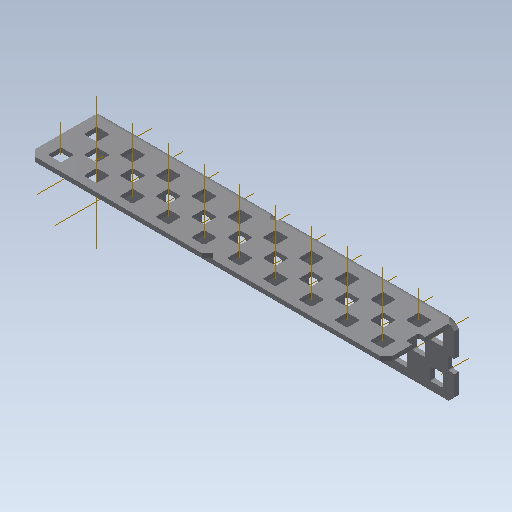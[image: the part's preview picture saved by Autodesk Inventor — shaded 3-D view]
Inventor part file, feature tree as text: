
AUTODESK INVENTOR PART (.ipt)
format: ipt  version: 2020 (Build 240168000, 168)  size: 1,934,336 bytes
history: native  units: in
note: dims shown in document units (in); Inventor stores cm internally (conversion verified against a paired STEP export)
features: other x65, pattern_linear x4, sheet_metal_op x1, extrude x1, imported_body x1, sketch x1
ambient origin geometry x8: Origin, YZ Plane, XZ Plane, XY Plane, X Axis, Y Axis, Z Axis, Center Point
bodies: Body1 (feature_tree)
feature tree (73):
  sheet_metal_op  "Fold1"
  other  "L-Channel"
  extrude  "length cut"  Depth=0.5in
  other  "top out axis"
  other  "top inner axis"
  other  "back out axis"
  other  "back inner axis"
  pattern_linear  "top outer axes"  Count1=2 Spacing1=0.5in
  pattern_linear  "top inner axes"  Spacing1=0.5in  [1 undecoded]
  pattern_linear  "back outer axes"  Count1=2 Spacing1=0.5in
  pattern_linear  "back inner axes"  Spacing1=0.5in  [1 undecoded]
  other  "right plane"
  imported_body  "Base1"
  sketch  "Sketch1"  dims[d1=0.0in d4=0.5in d5=0.7874in d7=0.5in d10=0.5in d13=0.5in d14=0.7874in d16=0.5in d19=0.5in d20=-5.0in d21=0.0in d22=0.0in d23=0.0in d24=0.0in d25=0.0in d26=0.0in]
  other  "Work Point1"
  other  "Work Point2"
  other  "Work Point3"
  other  "Work Point4"
  other  "Work Axis5"
  other  "Work Axis6"
  other  "Work Axis7"
  other  "Work Axis8"
  other  "Work Axis11"
  other  "Work Axis12"
  other  "Work Axis13"
  other  "Work Axis14"
  other  "Work Axis15"
  other  "Work Axis18"
  other  "Work Axis19"
  other  "Work Axis20"
  other  "Work Axis23"
  other  "Work Axis24"
  other  "Work Axis25"
  other  "Work Axis26"
  other  "Work Axis29"
  other  "Work Axis30"
  other  "Work Axis31"
  other  "Work Axis32"
  other  "Work Axis33"
  other  "Work Axis36"
  other  "Work Axis37"
  other  "Work Axis38"
  other  "Work Axis41"
  other  "Work Axis42"
  other  "Work Axis43"
  other  "Work Axis44"
  other  "Work Axis45"
  other  "Work Axis61"
  other  "Work Axis62"
  other  "Work Axis63"
  other  "Work Axis64"
  other  "Work Axis65"
  other  "Work Axis81"
  other  "Work Axis82"
  other  "Work Axis83"
  other  "Work Axis84"
  other  "Work Axis85"
  other  "Work Axis101"
  other  "Work Axis102"
  other  "Work Axis103"
  other  "Work Axis104"
  other  "Work Axis105"
  other  "Work Axis121"
  other  "Work Axis122"
  other  "Work Axis123"
  other  "Work Axis124"
  other  "Work Axis125"
  other  "Work Axis141"
  other  "Work Axis142"
  other  "Work Axis143"
  other  "Work Axis144"
  other  "Work Axis145"
  other  "left plane"
note: 2 required parameter values undecoded (feature->parameter linkage not recoverable at this tier; creation-order binding heuristic only, values carry confidence <= 0.55)
